# Revit family: Legrand XL³-S 630 36 módulos a la fila
name_source: partatom
category: Equipement électrique
units: mm (PartAtom-declared; Revit-internal decimal feet)

## family parameters
Basée sur le plan de construction = Non
Configuration du panneau = Deux colonnes, circuits au sein
Cote de connecteur circulaire = Utiliser le diamètre
Couper avec des vides une fois chargée = Non
Numéro OmniClass = 23.80.30.11.17
Partagée = Non
Point de calcul de pièce = Non
Titre OmniClass = Distribution Boards and Control Panels
Toujours verticalement = Oui
Type d'élément = Tableau de raccordement

## types (11) — shared parameters
Altura Básica = 100 mm  [stored 0.328084 ft]
Fabricant = Legrand
IK = 08
IP = 40
Image du type = XL3S_630_36M_337583_p_230131.jpg
Materia = Acero
RAL = 9003
URL = www.legrand.fr
anchura = 804 mm  [stored 2.6378 ft]
anchura asentamiento = 1302 mm  [stored 4.27165 ft]
base = Oui
distancia antes de asentamiento = 804 mm  [stored 2.6378 ft]
distancia lado asentamiento = 249 mm  [stored 0.816929 ft]
kit acabado = Non
kit acabado 337960_337974 = Non
kit acabado 337961_337974 = Non
kit acabado 337962_337974 = Non
kit acabado 337963_337974 = Non
kit acabado 337964_337974 = Non
kit acabado 337965_337974 = Non
kit acabado 337966_337974 = Non
kit acabado 337967_337974 = Non
kit acabado 337968_337974 = Non
kit acabado 337969_337974 = Non
kit acabado 337970_337974 = Non
panele lateral derecho = Oui
panele lateral izquierdo = Oui
profundidad = 249 mm  [stored 0.816929 ft]
profundidad asentamiento = 1053 mm
puerta = Oui
zero-valued in all types: Elévation par défaut

## per-type parameters (varying)
- Envolvente de distribución - XL³ S 630 -  Metal - altura 750 - 36 módulos: Altura=924 mm  [stored 3.0315 ft]; Condiciones Generales de Uso=https://export.legrand.com; Description=Ref 337523 - Envolvente de distribución - XL³ S 630 -  Metal - altura 750 - 36 módulos; envoltura 337523=Oui; envoltura 337533=Non; envoltura 337543=Non; envoltura 337553=Non; envoltura 337563=Non; envoltura 337573=Non; envoltura 337583=Non; envoltura 337593=Non; envoltura 337603=Non; envoltura 337613=Non; envoltura 337623=Non; panele lateral derecho 337862=Oui; panele lateral derecho 337863=Non; panele lateral derecho 337864=Non; panele lateral derecho 337865=Non; panele lateral derecho 337866=Non; panele lateral derecho 337867=Non; panele lateral derecho 337868=Non; panele lateral derecho 337869=Non; panele lateral derecho 337870=Non; panele lateral derecho 337871=Non; panele lateral derecho 337872=Non; panele lateral izquierdo 337862=Oui; panele lateral izquierdo 337863=Non; panele lateral izquierdo 337864=Non; panele lateral izquierdo 337865=Non; panele lateral izquierdo 337866=Non; panele lateral izquierdo 337867=Non; panele lateral izquierdo 337868=Non; panele lateral izquierdo 337869=Non; panele lateral izquierdo 337870=Non; panele lateral izquierdo 337871=Non; panele lateral izquierdo 337872=Non; puerta 337643=Oui; puerta 337653=Non; puerta 337663=Non; puerta 337673=Non; puerta 337683=Non; puerta 337693=Non; puerta 337703=Non; puerta 337713=Non; puerta 337723=Non; puerta 337733=Non; puerta 337743=Non
- Envolvente de distribución - XL³ S 630 -  Metal - altura 900 - 36 módulos: Altura=1074 mm  [stored 3.52362 ft]; Condiciones Generales de Uso=https://export.legrand.com; Description=Ref 337533 - Envolvente de distribución - XL³ S 630 -  Metal - altura 900 - 36 módulos; envoltura 337523=Non; envoltura 337533=Oui; envoltura 337543=Non; envoltura 337553=Non; envoltura 337563=Non; envoltura 337573=Non; envoltura 337583=Non; envoltura 337593=Non; envoltura 337603=Non; envoltura 337613=Non; envoltura 337623=Non; panele lateral derecho 337862=Non; panele lateral derecho 337863=Oui; panele lateral derecho 337864=Non; panele lateral derecho 337865=Non; panele lateral derecho 337866=Non; panele lateral derecho 337867=Non; panele lateral derecho 337868=Non; panele lateral derecho 337869=Non; panele lateral derecho 337870=Non; panele lateral derecho 337871=Non; panele lateral derecho 337872=Non; panele lateral izquierdo 337862=Non; panele lateral izquierdo 337863=Oui; panele lateral izquierdo 337864=Non; panele lateral izquierdo 337865=Non; panele lateral izquierdo 337866=Non; panele lateral izquierdo 337867=Non; panele lateral izquierdo 337868=Non; panele lateral izquierdo 337869=Non; panele lateral izquierdo 337870=Non; panele lateral izquierdo 337871=Non; panele lateral izquierdo 337872=Non; puerta 337643=Non; puerta 337653=Oui; puerta 337663=Non; puerta 337673=Non; puerta 337683=Non; puerta 337693=Non; puerta 337703=Non; puerta 337713=Non; puerta 337723=Non; puerta 337733=Non; puerta 337743=Non
- Envolvente de distribución - XL³ S 630 -  Metal - altura 1050 - 36 módulos: Altura=1224 mm  [stored 4.01575 ft]; Condiciones Generales de Uso=https://export.legrand.com; Description=Ref 337543 - Envolvente de distribución - XL³ S 630 -  Metal - altura 1050 - 36 módulos; envoltura 337523=Non; envoltura 337533=Non; envoltura 337543=Oui; envoltura 337553=Non; envoltura 337563=Non; envoltura 337573=Non; envoltura 337583=Non; envoltura 337593=Non; envoltura 337603=Non; envoltura 337613=Non; envoltura 337623=Non; panele lateral derecho 337862=Non; panele lateral derecho 337863=Non; panele lateral derecho 337864=Oui; panele lateral derecho 337865=Non; panele lateral derecho 337866=Non; panele lateral derecho 337867=Non; panele lateral derecho 337868=Non; panele lateral derecho 337869=Non; panele lateral derecho 337870=Non; panele lateral derecho 337871=Non; panele lateral derecho 337872=Non; panele lateral izquierdo 337862=Non; panele lateral izquierdo 337863=Non; panele lateral izquierdo 337864=Oui; panele lateral izquierdo 337865=Non; panele lateral izquierdo 337866=Non; panele lateral izquierdo 337867=Non; panele lateral izquierdo 337868=Non; panele lateral izquierdo 337869=Non; panele lateral izquierdo 337870=Non; panele lateral izquierdo 337871=Non; panele lateral izquierdo 337872=Non; puerta 337643=Non; puerta 337653=Non; puerta 337663=Oui; puerta 337673=Non; puerta 337683=Non; puerta 337693=Non; puerta 337703=Non; puerta 337713=Non; puerta 337723=Non; puerta 337733=Non; puerta 337743=Non
- Envolvente de distribución - XL³ S 630 -  Metal - altura 1200 - 36 módulos: Altura=1374 mm  [stored 4.50787 ft]; Condiciones Generales de Uso=https://export.legrand.com; Description=Ref 337553 - Envolvente de distribución - XL³ S 630 -  Metal - altura 1200 - 36 módulos; envoltura 337523=Non; envoltura 337533=Non; envoltura 337543=Non; envoltura 337553=Oui; envoltura 337563=Non; envoltura 337573=Non; envoltura 337583=Non; envoltura 337593=Non; envoltura 337603=Non; envoltura 337613=Non; envoltura 337623=Non; panele lateral derecho 337862=Non; panele lateral derecho 337863=Non; panele lateral derecho 337864=Non; panele lateral derecho 337865=Oui; panele lateral derecho 337866=Non; panele lateral derecho 337867=Non; panele lateral derecho 337868=Non; panele lateral derecho 337869=Non; panele lateral derecho 337870=Non; panele lateral derecho 337871=Non; panele lateral derecho 337872=Non; panele lateral izquierdo 337862=Non; panele lateral izquierdo 337863=Non; panele lateral izquierdo 337864=Non; panele lateral izquierdo 337865=Oui; panele lateral izquierdo 337866=Non; panele lateral izquierdo 337867=Non; panele lateral izquierdo 337868=Non; panele lateral izquierdo 337869=Non; panele lateral izquierdo 337870=Non; panele lateral izquierdo 337871=Non; panele lateral izquierdo 337872=Non; puerta 337643=Non; puerta 337653=Non; puerta 337663=Non; puerta 337673=Oui; puerta 337683=Non; puerta 337693=Non; puerta 337703=Non; puerta 337713=Non; puerta 337723=Non; puerta 337733=Non; puerta 337743=Non
- Envolvente de distribución - XL³ S 630 -  Metal - altura 1350 - 36 módulos: Altura=1524 mm  [stored 5 ft]; Condiciones Generales de Uso=https://export.legrand.com; Description=Ref 337563 -Envolvente de distribución - XL³ S 630 -  Metal - altura 1350 - 36 módulos; envoltura 337523=Non; envoltura 337533=Non; envoltura 337543=Non; envoltura 337553=Non; envoltura 337563=Oui; envoltura 337573=Non; envoltura 337583=Non; envoltura 337593=Non; envoltura 337603=Non; envoltura 337613=Non; envoltura 337623=Non; panele lateral derecho 337862=Non; panele lateral derecho 337863=Non; panele lateral derecho 337864=Non; panele lateral derecho 337865=Non; panele lateral derecho 337866=Oui; panele lateral derecho 337867=Non; panele lateral derecho 337868=Non; panele lateral derecho 337869=Non; panele lateral derecho 337870=Non; panele lateral derecho 337871=Non; panele lateral derecho 337872=Non; panele lateral izquierdo 337862=Non; panele lateral izquierdo 337863=Non; panele lateral izquierdo 337864=Non; panele lateral izquierdo 337865=Non; panele lateral izquierdo 337866=Oui; panele lateral izquierdo 337867=Non; panele lateral izquierdo 337868=Non; panele lateral izquierdo 337869=Non; panele lateral izquierdo 337870=Non; panele lateral izquierdo 337871=Non; panele lateral izquierdo 337872=Non; puerta 337643=Non; puerta 337653=Non; puerta 337663=Non; puerta 337673=Non; puerta 337683=Oui; puerta 337693=Non; puerta 337703=Non; puerta 337713=Non; puerta 337723=Non; puerta 337733=Non; puerta 337743=Non
- Envolvente de distribución - XL³ S 630 -  Metal - altura 1500 - 36 módulos: Altura=1674 mm  [stored 5.49213 ft]; Description=Ref 337573 -Envolvente de distribución - XL³ S 630 -  Metal - altura 1500 - 36 módulos; envoltura 337523=Non; envoltura 337533=Non; envoltura 337543=Non; envoltura 337553=Non; envoltura 337563=Non; envoltura 337573=Oui; envoltura 337583=Non; envoltura 337593=Non; envoltura 337603=Non; envoltura 337613=Non; envoltura 337623=Non; panele lateral derecho 337862=Non; panele lateral derecho 337863=Non; panele lateral derecho 337864=Non; panele lateral derecho 337865=Non; panele lateral derecho 337866=Non; panele lateral derecho 337867=Oui; panele lateral derecho 337868=Non; panele lateral derecho 337869=Non; panele lateral derecho 337870=Non; panele lateral derecho 337871=Non; panele lateral derecho 337872=Non; panele lateral izquierdo 337862=Non; panele lateral izquierdo 337863=Non; panele lateral izquierdo 337864=Non; panele lateral izquierdo 337865=Non; panele lateral izquierdo 337866=Non; panele lateral izquierdo 337867=Oui; panele lateral izquierdo 337868=Non; panele lateral izquierdo 337869=Non; panele lateral izquierdo 337870=Non; panele lateral izquierdo 337871=Non; panele lateral izquierdo 337872=Non; puerta 337643=Non; puerta 337653=Non; puerta 337663=Non; puerta 337673=Non; puerta 337683=Non; puerta 337693=Oui; puerta 337703=Non; puerta 337713=Non; puerta 337723=Non; puerta 337733=Non; puerta 337743=Non
- Envolvente de distribución - XL³ S 630 -  Metal - altura 1650 - 36 módulos: Altura=1824 mm  [stored 5.98425 ft]; Condiciones Generales de Uso=https://export.legrand.com; Description=Ref 337583 - Envolvente de distribución - XL³ S 630 -  Metal - altura 1650 - 36 módulos; envoltura 337523=Non; envoltura 337533=Non; envoltura 337543=Non; envoltura 337553=Non; envoltura 337563=Non; envoltura 337573=Non; envoltura 337583=Oui; envoltura 337593=Non; envoltura 337603=Non; envoltura 337613=Non; envoltura 337623=Non; panele lateral derecho 337862=Non; panele lateral derecho 337863=Non; panele lateral derecho 337864=Non; panele lateral derecho 337865=Non; panele lateral derecho 337866=Non; panele lateral derecho 337867=Non; panele lateral derecho 337868=Oui; panele lateral derecho 337869=Non; panele lateral derecho 337870=Non; panele lateral derecho 337871=Non; panele lateral derecho 337872=Non; panele lateral izquierdo 337862=Non; panele lateral izquierdo 337863=Non; panele lateral izquierdo 337864=Non; panele lateral izquierdo 337865=Non; panele lateral izquierdo 337866=Non; panele lateral izquierdo 337867=Non; panele lateral izquierdo 337868=Oui; panele lateral izquierdo 337869=Non; panele lateral izquierdo 337870=Non; panele lateral izquierdo 337871=Non; panele lateral izquierdo 337872=Non; puerta 337643=Non; puerta 337653=Non; puerta 337663=Non; puerta 337673=Non; puerta 337683=Non; puerta 337693=Non; puerta 337703=Oui; puerta 337713=Non; puerta 337723=Non; puerta 337733=Non; puerta 337743=Non
- Envolvente de distribución - XL³ S 630 -  Metal - altura 1800 - 36 módulos: Altura=1974 mm  [stored 6.47638 ft]; Condiciones Generales de Uso=https://export.legrand.com; Description=Ref 337593 - Envolvente de distribución - XL³ S 630 -  Metal - altura 1800 - 36 módulos; envoltura 337523=Non; envoltura 337533=Non; envoltura 337543=Non; envoltura 337553=Non; envoltura 337563=Non; envoltura 337573=Non; envoltura 337583=Non; envoltura 337593=Oui; envoltura 337603=Non; envoltura 337613=Non; envoltura 337623=Non; panele lateral derecho 337862=Non; panele lateral derecho 337863=Non; panele lateral derecho 337864=Non; panele lateral derecho 337865=Non; panele lateral derecho 337866=Non; panele lateral derecho 337867=Non; panele lateral derecho 337868=Non; panele lateral derecho 337869=Oui; panele lateral derecho 337870=Non; panele lateral derecho 337871=Non; panele lateral derecho 337872=Non; panele lateral izquierdo 337862=Non; panele lateral izquierdo 337863=Non; panele lateral izquierdo 337864=Non; panele lateral izquierdo 337865=Non; panele lateral izquierdo 337866=Non; panele lateral izquierdo 337867=Non; panele lateral izquierdo 337868=Non; panele lateral izquierdo 337869=Oui; panele lateral izquierdo 337870=Non; panele lateral izquierdo 337871=Non; panele lateral izquierdo 337872=Non; puerta 337643=Non; puerta 337653=Non; puerta 337663=Non; puerta 337673=Non; puerta 337683=Non; puerta 337693=Non; puerta 337703=Non; puerta 337713=Oui; puerta 337723=Non; puerta 337733=Non; puerta 337743=Non
- Envolvente de distribución - XL³ S 630 -  Metal - altura 1950 - 36 módulos: Altura=2124 mm  [stored 6.9685 ft]; Condiciones Generales de Uso=https://export.legrand.com; Description=Ref 337603 - Envolvente de distribución - XL³ S 630 -  Metal - altura 1950 - 36 módulos; envoltura 337523=Non; envoltura 337533=Non; envoltura 337543=Non; envoltura 337553=Non; envoltura 337563=Non; envoltura 337573=Non; envoltura 337583=Non; envoltura 337593=Non; envoltura 337603=Oui; envoltura 337613=Non; envoltura 337623=Non; panele lateral derecho 337862=Non; panele lateral derecho 337863=Non; panele lateral derecho 337864=Non; panele lateral derecho 337865=Non; panele lateral derecho 337866=Non; panele lateral derecho 337867=Non; panele lateral derecho 337868=Non; panele lateral derecho 337869=Non; panele lateral derecho 337870=Oui; panele lateral derecho 337871=Non; panele lateral derecho 337872=Non; panele lateral izquierdo 337862=Non; panele lateral izquierdo 337863=Non; panele lateral izquierdo 337864=Non; panele lateral izquierdo 337865=Non; panele lateral izquierdo 337866=Non; panele lateral izquierdo 337867=Non; panele lateral izquierdo 337868=Non; panele lateral izquierdo 337869=Non; panele lateral izquierdo 337870=Oui; panele lateral izquierdo 337871=Non; panele lateral izquierdo 337872=Non; puerta 337643=Non; puerta 337653=Non; puerta 337663=Non; puerta 337673=Non; puerta 337683=Non; puerta 337693=Non; puerta 337703=Non; puerta 337713=Non; puerta 337723=Oui; puerta 337733=Non; puerta 337743=Non
- Envolvente de distribución - XL³ S 630 -  Metal - altura 2100 - 36 módulos: Altura=2274 mm  [stored 7.46063 ft]; Condiciones Generales de Uso=https://export.legrand.com; Description=Ref 337613 - Envolvente de distribución - XL³ S 630 -  Metal - altura 2100 - 36 módulos; envoltura 337523=Non; envoltura 337533=Non; envoltura 337543=Non; envoltura 337553=Non; envoltura 337563=Non; envoltura 337573=Non; envoltura 337583=Non; envoltura 337593=Non; envoltura 337603=Non; envoltura 337613=Oui; envoltura 337623=Non; panele lateral derecho 337862=Non; panele lateral derecho 337863=Non; panele lateral derecho 337864=Non; panele lateral derecho 337865=Non; panele lateral derecho 337866=Non; panele lateral derecho 337867=Non; panele lateral derecho 337868=Non; panele lateral derecho 337869=Non; panele lateral derecho 337870=Non; panele lateral derecho 337871=Oui; panele lateral derecho 337872=Non; panele lateral izquierdo 337862=Non; panele lateral izquierdo 337863=Non; panele lateral izquierdo 337864=Non; panele lateral izquierdo 337865=Non; panele lateral izquierdo 337866=Non; panele lateral izquierdo 337867=Non; panele lateral izquierdo 337868=Non; panele lateral izquierdo 337869=Non; panele lateral izquierdo 337870=Non; panele lateral izquierdo 337871=Oui; panele lateral izquierdo 337872=Non; puerta 337643=Non; puerta 337653=Non; puerta 337663=Non; puerta 337673=Non; puerta 337683=Non; puerta 337693=Non; puerta 337703=Non; puerta 337713=Non; puerta 337723=Non; puerta 337733=Oui; puerta 337743=Non
- Envolvente de distribución - XL³ S 630 -  Metal - altura 2250 - 36 módulos: Altura=2424 mm  [stored 7.95276 ft]; Condiciones Generales de Uso=https://export.legrand.com; Description=Ref 337623 - Envolvente de distribución - XL³ S 630 -  Metal - altura 2250 - 36 módulos; envoltura 337523=Non; envoltura 337533=Non; envoltura 337543=Non; envoltura 337553=Non; envoltura 337563=Non; envoltura 337573=Non; envoltura 337583=Non; envoltura 337593=Non; envoltura 337603=Non; envoltura 337613=Non; envoltura 337623=Oui; panele lateral derecho 337862=Non; panele lateral derecho 337863=Non; panele lateral derecho 337864=Non; panele lateral derecho 337865=Non; panele lateral derecho 337866=Non; panele lateral derecho 337867=Non; panele lateral derecho 337868=Non; panele lateral derecho 337869=Non; panele lateral derecho 337870=Non; panele lateral derecho 337871=Non; panele lateral derecho 337872=Oui; panele lateral izquierdo 337862=Non; panele lateral izquierdo 337863=Non; panele lateral izquierdo 337864=Non; panele lateral izquierdo 337865=Non; panele lateral izquierdo 337866=Non; panele lateral izquierdo 337867=Non; panele lateral izquierdo 337868=Non; panele lateral izquierdo 337869=Non; panele lateral izquierdo 337870=Non; panele lateral izquierdo 337871=Non; panele lateral izquierdo 337872=Oui; puerta 337643=Non; puerta 337653=Non; puerta 337663=Non; puerta 337673=Non; puerta 337683=Non; puerta 337693=Non; puerta 337703=Non; puerta 337713=Non; puerta 337723=Non; puerta 337733=Non; puerta 337743=Oui

note: [stored X ft] marks values corroborated as IEEE doubles in the binary element streams (Revit-internal decimal feet)
